# Revit family: Site-Fencing-Tymetal_Corp-Box_Frame_Cantilever_Slide_Gate-Ornamental-TYM-VS2-1
name_source: partatom
category: Site
revit_build: Autodesk Revit 2015 (Build: 20140606_1530(x64)
units: mm (PartAtom-declared; Revit-internal decimal feet)

## types (2) — shared parameters
Apparent Load Phase1 = 746 VA
Apparent Load Phase2 = 746 VA
Apparent Load Phase3 = 746 VA
Assembly Code = G2040100
Back Picket Count per Panel = 22
Back Picket Panel Count = 4
Back Picket Panel Length = 5' - 7 1/4"
Back Picket Spacing = 0' - 3"
Back Support Picket = 3
Between Posts = 2' - 11"
Bottom Guide Cover = No
Catch Assembly Height above Grade = 3' - 6"
Clear Opening = 15' - 0"
Connector Description = Connection for Electrical Power
Counter Balance Length = 7' - 6"
Description = TYM-VS2-1B Operator on a Fortress Box Frame Cantilever Slide Gate with Ornamental Fencing
Drive Type = #50 Chain
Fence Offset from Grade = 0' - 5"
Finish = Metal - Tymetal - Aluminum
Finish Note = For additional powder coat color options, please contact Tymetal
Frame Width = 0' - 2"
Front Picket Count per Panel = 20
Front Picket Panel Count = 3
Front Picket Panel Length = 4' - 10 21/32"
Front Picket Spacing = 0' - 3"
Front Support Picket = 2
Gate Documentation Link = http://www.tymetal.com
Gate Height Clearances = 6' - 0"
Gate Opening (Max) = 60 ft
Gate Speed = 2 ft / sec
Gate Weight (Max) = 2500 lbs
Hardware Finish = Metal - Tymetal - Aluminum
Height = 6' - 0"
Length = 22' - 6"
Load Classification = Power
Manufacturer = Tymetal Corp.
Maximum Cycles = Continuous Duty
Model = Ornamental
Mount Clamp Extension from Gate = 0' - 2"
Nominal Height = 6' - 6"
Notes = Single Clear Opening up to 60' and Double Clear Openings up to 120'
Operator Documentation Link = http://www.tymetal.com
Operator Finish = Plastic - Tymetal - Polyethylene - Black
Pad Finish = Concrete - Tymetal - Cast-In-Place - Gray
Pad Note = OPERATOR PAD DEPTH TO BE MINIMUM OF 24IN AND IN ACCORDANCE WITH ALL LOCAL CODES AND SOIL CONDITIONS.
Phase = 1
Picket Height = 0' - 6"
Picket Top = Yes
Post Diameter = 0' - 4"
Post Height = 6' - 6"
Post Radius = 0' - 2"
Post Spacing = 6' - 7"
Product Documentation Link = http://www.tymetal.com
Product Page URL = http://www.tymetal.com
Product data url = https://bimobject.com
Single Gate Clearances = 15' - 0"
URL = http://www.tymetal.com
Watts = 746 W

## per-type parameters (varying)
| type | Number of Poles | Power Factor | Voltage |
| Single Phase | 1 | 1 | 230 V |
| Three Phase | 3 | 0.8 | 460 V |

## geometry (parser evidence)
native form markers: Sweep x57
no freeform markers — native parametric forms only
